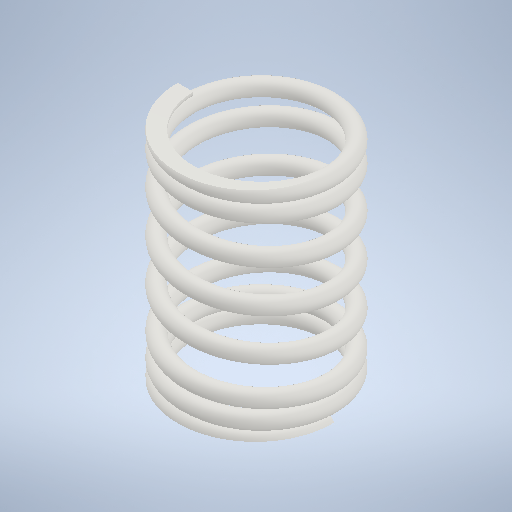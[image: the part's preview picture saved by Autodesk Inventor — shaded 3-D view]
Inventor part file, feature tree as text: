
AUTODESK INVENTOR PART (.ipt)
format: ipt  version: 2025 (Build 290162010, 162A)  size: 1,084,416 bytes
history: native  units: mm
features: other x65, extrude x8, plane x5, sketch x5, helix x3, sweep x2, projected_geometry x1
ambient origin geometry x8: Origin, YZ Plane, XZ Plane, XY Plane, X Axis, Y Axis, Z Axis, Center Point
bodies: Body1 (feature_tree), Body2 (feature_tree), Body3 (feature_tree)
feature tree (89):
  other  "Hauptschraubenpfad(Rechts)"
  other  "Profilarbeitsebene(Rechts)"
  plane  "Arbeitsebene(Rechts) starten"
  plane  "Arbeitsebene(Rechts) beenden"
  other  "Schnittarbeitsebene(Rechts) beenden"
  other  "Schnittarbeitsebene(Rechts) starten"
  other  "Schnittarbeitsebene mit flachen Enden 1(Rechts)"
  other  "Schnittarbeitsebene mit flachen Enden 2(Rechts)"
  sweep  "Main Coil Feature(R)"
  other  "Übergangsschraube 1(Rechts) starten"
  helix  "Coil  Start Transition 2(R)"  [1 undecoded]
  helix  "Coil  Start Transition 3(R)"  [1 undecoded]
  helix  "Coil  Start Transition 4(R)"  [1 undecoded]
  other  "Endenschraube(Rechts) starten"
  extrude  "Schnittelement(Rechts) starten"  Depth=10.0mm
  other  "Übergangsschraube 1(Rechts) beenden"
  other  "Übergangsschraube 2(Rechts) beenden"
  other  "Übergangsschraube 3(Rechts) beenden"
  other  "Übergangsschraube 4(Rechts) beenden"
  other  "Spirale(Rechts) beenden"
  extrude  "Schnittelement(Rechts) beenden"  Depth=10.0mm
  extrude  "Schnittelement mit flachen Enden 1(Rechts)"  Depth=10.0mm
  extrude  "Plain Ends Cut  2(R)"  Depth=10.0mm TaperAngle=0.0deg
  other  "Hauptschraubenpfad(Links)"
  other  "Profilarbeitsebene(Links)"
  plane  "Arbeitsebene(Links) starten"
  plane  "Arbeitsebene(Links) beenden"
  other  "Schnittarbeitsebene(Links) beenden"
  other  "Schnittarbeitsebene(Links) starten"
  other  "Schnittarbeitsebene mit flachen Enden 1(Links)"
  other  "Schnittarbeitsebene mit flachen Enden 2(Links)"
  sweep  "Main Coil Feature(L)"
  other  "Übergangsschraube 1(Links) starten"
  other  "Übergangsschraube 2(Links) starten"
  other  "Übergangsschraube 3(Links) starten"
  other  "Übergangsschraube 4(Links) starten"
  other  "Endenschraube(Links) starten"
  extrude  "Schnittelement(Links) starten"  Depth=10.0mm TaperAngle=0.0deg
  other  "Übergangsschraube 1(Links) beenden"
  other  "Übergangsschraube 2(Links) beenden"
  other  "Übergangsschraube 3(Links) beenden"
  other  "Übergangsschraube 4(Links) beenden"
  other  "Spirale(Links) beenden"
  extrude  "Schnittelement(Links) beenden"  Depth=10.0mm
  extrude  "Cut Plain Ends Cut 1(L)"  Depth=10.0mm
  extrude  "Cut Plain Ends Cut 2(L)"  Depth=10.0mm
  other  "iMate-basierte Arbeitsebene"
  other  "Vorschau Mittelpunkt"
  other  "Vorschau X-Achse"
  sketch  "Sketch39"  dims[d0=0.2mm d2=2.130968mm d3=10.0mm d4=32.5mm]
  sketch  "Sketch40"  dims[d5=0.0mm d6=90.0deg d7=90.0deg d8=0.0mm d9=0.0mm d12=1.774342mm d13=-2.300006mm d14=0.8mm]
  other  "Pfadprofilskizze(Rechts)"
  other  "Srf1"
  other  "Spiralenprofilskizze(Rechts)"
  other  "Übergangsschraubenskizze 1(Rechts) starten"
  sketch  "Sketch  Start Transition 2(R)"  dims[d15=0.0mm]
  sketch  "Sketch  Start Transition 3(R)"  dims[d16=1.798226mm d17=10.0mm d18=2.5mm d19=0.0mm d20=90.0deg d21=90.0deg d22=0.0mm d23=0.0mm]
  sketch  "Sketch  Start Transition 4(R)"  dims[d24=1.465484mm d25=10.0mm d26=2.5mm d27=0.0mm d28=90.0deg d29=90.0deg d30=0.0mm d31=0.0mm d32=1.132742mm d33=10.0mm d34=2.5mm d35=0.0mm d36=90.0deg d37=90.0deg d38=0.0mm d39=0.0mm d40=0.8mm d41=10.0mm d42=2.5mm d43=0.0mm d44=90.0deg d45=90.0deg d46=0.0mm d47=0.0mm d48=1.798226mm d49=10.0mm d50=1.875mm d51=0.0mm d52=90.0deg d53=90.0deg d54=0.0mm d55=0.0mm d56=1.465484mm d57=10.0mm d58=1.875mm d59=0.0mm d60=90.0deg d61=90.0deg d62=0.0mm d63=0.0mm d64=1.132742mm d65=10.0mm d66=1.875mm d67=0.0mm d68=90.0deg d69=90.0deg d70=0.0mm d71=0.0mm d72=0.8mm d73=10.0mm d74=1.875mm d75=0.0mm d76=90.0deg d77=90.0deg d78=0.0mm d79=0.0mm d81=10.0mm d82=15.0mm d83=0.0mm d84=90.0deg d85=90.0deg d86=0.0mm d87=0.0mm d88=0.803542mm d89=10.0mm d90=10.0mm d91=0.0mm d92=90.0deg d93=90.0deg d94=0.0mm d95=0.0mm d96=8.0mm d97=0.803542mm d98=0.0mm d99=8.0mm d100=0.803542mm d101=0.0mm d102=0.0mm d103=10.0mm d104=10.0mm d105=10.0mm d106=10.0mm d108=10.0mm d112=10.0mm d113=10.0mm d114=10.0mm d121=0.20442mm d131=10.0mm d132=10.0mm d133=10.0mm d134=10.0mm d135=0.2mm d137=2.130968mm d138=10.0mm d139=32.5mm d140=0.0mm d141=90.0deg d142=90.0deg d143=0.0mm d144=0.0mm d145=1.774342mm d146=-2.300006mm d147=0.20442mm d148=0.003535mm d149=0.8mm d150=0.0mm d151=0.0mm d152=1.798226mm d153=10.0mm d154=2.5mm d155=0.0mm d156=90.0deg d157=90.0deg d158=0.0mm d159=0.0mm d160=1.465484mm d161=10.0mm d162=2.5mm d163=0.0mm d164=90.0deg d165=90.0deg d166=0.0mm d167=0.0mm d168=1.132742mm d169=10.0mm d170=2.5mm d171=0.0mm d172=90.0deg d173=90.0deg d174=0.0mm d175=0.0mm d176=0.8mm d177=10.0mm d178=2.5mm d179=0.0mm d180=90.0deg d181=90.0deg d182=0.0mm d183=0.0mm d184=0.0mm d185=0.0mm d186=0.0mm d187=0.0mm d188=0.803542mm d189=10.0mm d190=15.0mm d191=0.0mm d192=90.0deg d193=90.0deg d194=0.0mm d195=0.0mm d196=0.0mm d197=8.0mm d198=0.803542mm d199=0.0mm d200=0.0mm d201=1.798226mm d202=10.0mm d203=1.875mm d204=0.0mm d205=90.0deg d206=90.0deg d207=0.0mm d208=0.0mm d209=0.0mm d210=1.465484mm d211=10.0mm d212=1.875mm d213=0.0mm d214=90.0deg d215=90.0deg d216=0.0mm d217=0.0mm d218=1.132742mm d219=10.0mm d220=1.875mm d221=0.0mm d222=90.0deg d223=90.0deg d224=0.0mm d225=0.0mm d226=0.8mm d227=10.0mm d228=1.875mm d229=0.0mm d230=90.0deg d231=90.0deg d232=0.0mm d233=0.0mm d234=0.0mm d235=0.0mm d236=0.0mm d237=0.803542mm d238=10.0mm d239=10.0mm d240=0.0mm d241=90.0deg d242=90.0deg d243=0.0mm d244=0.0mm d245=8.0mm d246=0.803542mm d247=0.0mm d248=0.0mm d249=0.0mm d254=8.0mm d255=10.0mm d256=0.0mm d257=10.0mm d258=-0.003535mm d259=8.0mm d260=10.0mm d261=0.0mm d262=20.0mm d263=8.0mm d264=10.0mm d265=0.0mm d266=20.0mm d267=0.0mm d270=-2.200006mm d271=0.0mm d272=8.0mm d273=10.0mm d274=0.0mm d275=10.0mm d276=157.079633mm d277=7.2mm d278=7.2mm d279=0.0mm d280=0.0mm d281=8.0mm d282=8.0mm]
  other  "Übergangsschraubenskizze 1(Rechts) beenden"
  other  "Übergangsschraubenskizze 2(Rechts) beenden"
  other  "Übergangsschraubenskizze 3(Rechts) beenden"
  other  "Übergangsschraubenskizze 4(Rechts) beenden"
  other  "Endenskizze(Rechts) starten"
  other  "Spiralenskizze(Rechts) beenden"
  other  "Schnittskizze(Rechts) beenden"
  other  "Schnittskizze (Rechts) starten"
  other  "Pfadprofilskizze(Links)"
  other  "Srf2"
  other  "Spiralenprofilskizze(Links)"
  other  "Übergangsschraubenskizze 1(Links) starten"
  other  "Übergangsschraubenskizze 2(Links) starten"
  other  "Übergangsschraubenskizze 3(Links) starten"
  other  "Übergangsschraubenskizze 4(Links) starten"
  other  "Endenskizze(Links) starten"
  other  "Schnittskizze(Links) starten"
  other  "Übergangsschraubenskizze 1(Links) beenden"
  other  "Übergangsschraubenskizze 2(Links) beenden"
  other  "Übergangsschraubenskizze 3(Links) beenden"
  other  "Übergangsschraubenskizze 4(Links) beenden"
  other  "Spiralenskizze(Links) beenden"
  other  "Schnittskizze(Links) beenden"
  other  "Schnittskizze mit flachen Enden 2(Links)"
  other  "Schnittskizze mit flachen Enden 2(Rechts)"
  other  "Schnittskizze mit flachen Enden 1(Rechts)"
  other  "Schnittskizze mit flachen Enden 1(Links)"
  plane  "Arbeitsebene - Schnitt starten"
  projected_geometry  "Projected Loop1"
  other  "Basiskurve(Rechts)"
  other  "Basiskurve(Links)"
note: 3 required parameter values undecoded (feature->parameter linkage not recoverable at this tier; creation-order binding heuristic only, values carry confidence <= 0.55)
